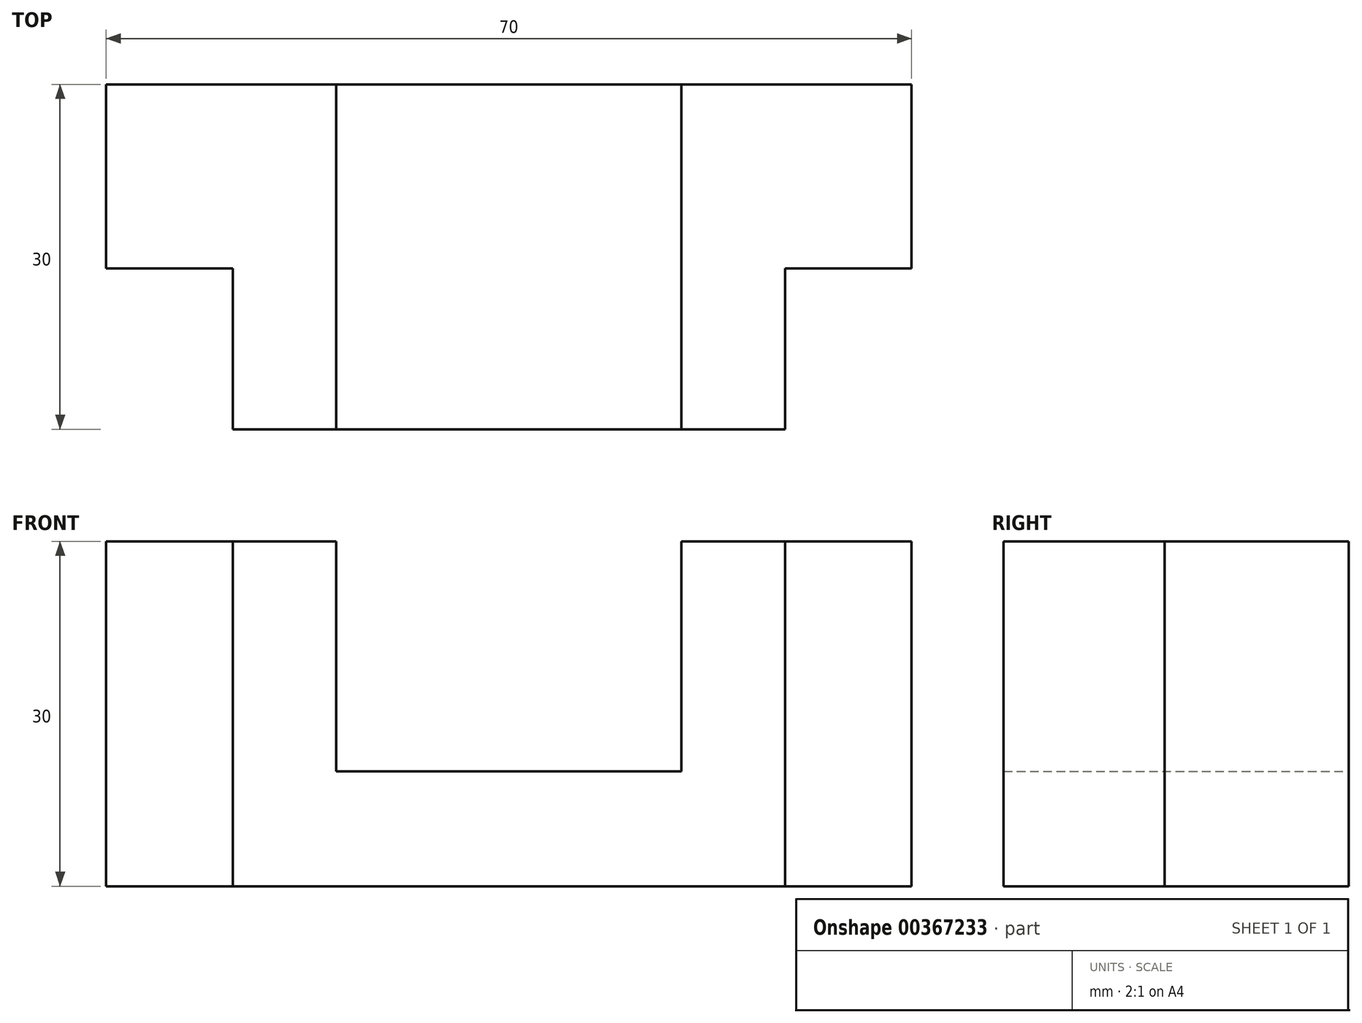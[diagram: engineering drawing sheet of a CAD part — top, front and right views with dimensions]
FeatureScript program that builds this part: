
annotation { "Feature Type Name" : "Feature", "Feature Type Description" : "" }
export const myFeature = defineFeature(function(context is Context, id is Id, definition is map)
    precondition{}
    {
        {
            var Q0;
            Q0=qCreatedBy(makeId("Front.planeOp"),FACE);
            var sketch = newSketch(context, id + "F0", { "sketchPlane" : qUnion([Q0])});
            skLineSegment(sketch, "E0", {"start": v(-35, 0) * mm, "end": v(35, 0) * mm});
            skLineSegment(sketch, "E1", {"start": v(35, 0) * mm, "end": v(35, 30) * mm});
            skLineSegment(sketch, "E2", {"start": v(35, 30) * mm, "end": v(15, 30) * mm});
            skLineSegment(sketch, "E3", {"start": v(15, 30) * mm, "end": v(15, 10) * mm});
            skLineSegment(sketch, "E4", {"start": v(15, 10) * mm, "end": v(-15, 10) * mm});
            skLineSegment(sketch, "E5", {"start": v(-15, 10) * mm, "end": v(-15, 30) * mm});
            skLineSegment(sketch, "E6", {"start": v(-15, 30) * mm, "end": v(-35, 30) * mm});
            skLineSegment(sketch, "E7", {"start": v(-35, 0) * mm, "end": v(-35, 30) * mm});
            skLineSegment(sketch, "E8", {"start": v(-25, 30) * mm, "end": v(-25, 0) * mm});
            skLineSegment(sketch, "E9", {"start": v(23, 0) * mm, "end": v(23, 30) * mm});
            skSolve(sketch);
        }
        {
            var Q0;
            Q0 = qSketchRegion(id + "F0", true);
            extrude(context, id + "F1", {"entities" : qUnion([Q0]), "depth" : 30 * mm});
        }
        {
            var Q0;
            Q0=qCreatedBy(makeId("Top.planeOp"),FACE);
            var sketch = newSketch(context, id + "F2", { "sketchPlane" : qUnion([Q0])});
            skLineSegment(sketch, "E10", {"start": v(-35, 0) * mm, "end": v(-35, -30) * mm});
            skLineSegment(sketch, "E11", {"start": v(-35, -30) * mm, "end": v(35, -30) * mm});
            skLineSegment(sketch, "E12", {"start": v(35, -30) * mm, "end": v(35, 0) * mm});
            skLineSegment(sketch, "E13", {"start": v(35, 0) * mm, "end": v(-35, 0) * mm});
            skLineSegment(sketch, "E14", {"start": v(-15, 0) * mm, "end": v(-15, -30) * mm});
            skLineSegment(sketch, "E15", {"start": v(15, -30) * mm, "end": v(15, 0) * mm});
            skLineSegment(sketch, "E16", {"start": v(-35, -16) * mm, "end": v(-24, -16) * mm});
            skLineSegment(sketch, "E17", {"start": v(-24, -16) * mm, "end": v(-24, -30) * mm});
            skLineSegment(sketch, "E18", {"start": v(24, -30) * mm, "end": v(24, -16) * mm});
            skLineSegment(sketch, "E19", {"start": v(24, -16) * mm, "end": v(35, -16) * mm});
            skSolve(sketch);
        }
        {
            var Q0;
            {var subQ3=sQuery(id+"F2.wireOp",EDGE,"E18");Q0=makeQuery(id+"F2.imprint","IMPRINT",FACE,{"disambiguationData":[TD([[makeQuery(id+"F2.imprint","IMPRINT",EDGE,{"derivedFrom":subQ3}),-1.0]])]});}
            var Q1;
            {var subQ3=sQuery(id+"F2.wireOp",EDGE,"E16");Q1=makeQuery(id+"F2.imprint","IMPRINT",FACE,{"disambiguationData":[TD([[makeQuery(id+"F2.imprint","IMPRINT",EDGE,{"derivedFrom":subQ3}),-1.0]])]});}
            extrude(context, id + "F3", {"entities" : qUnion([Q0, Q1]), "operationType" : NewBodyOperationType.REMOVE, "depth" : 30 * mm});
        }
    });
